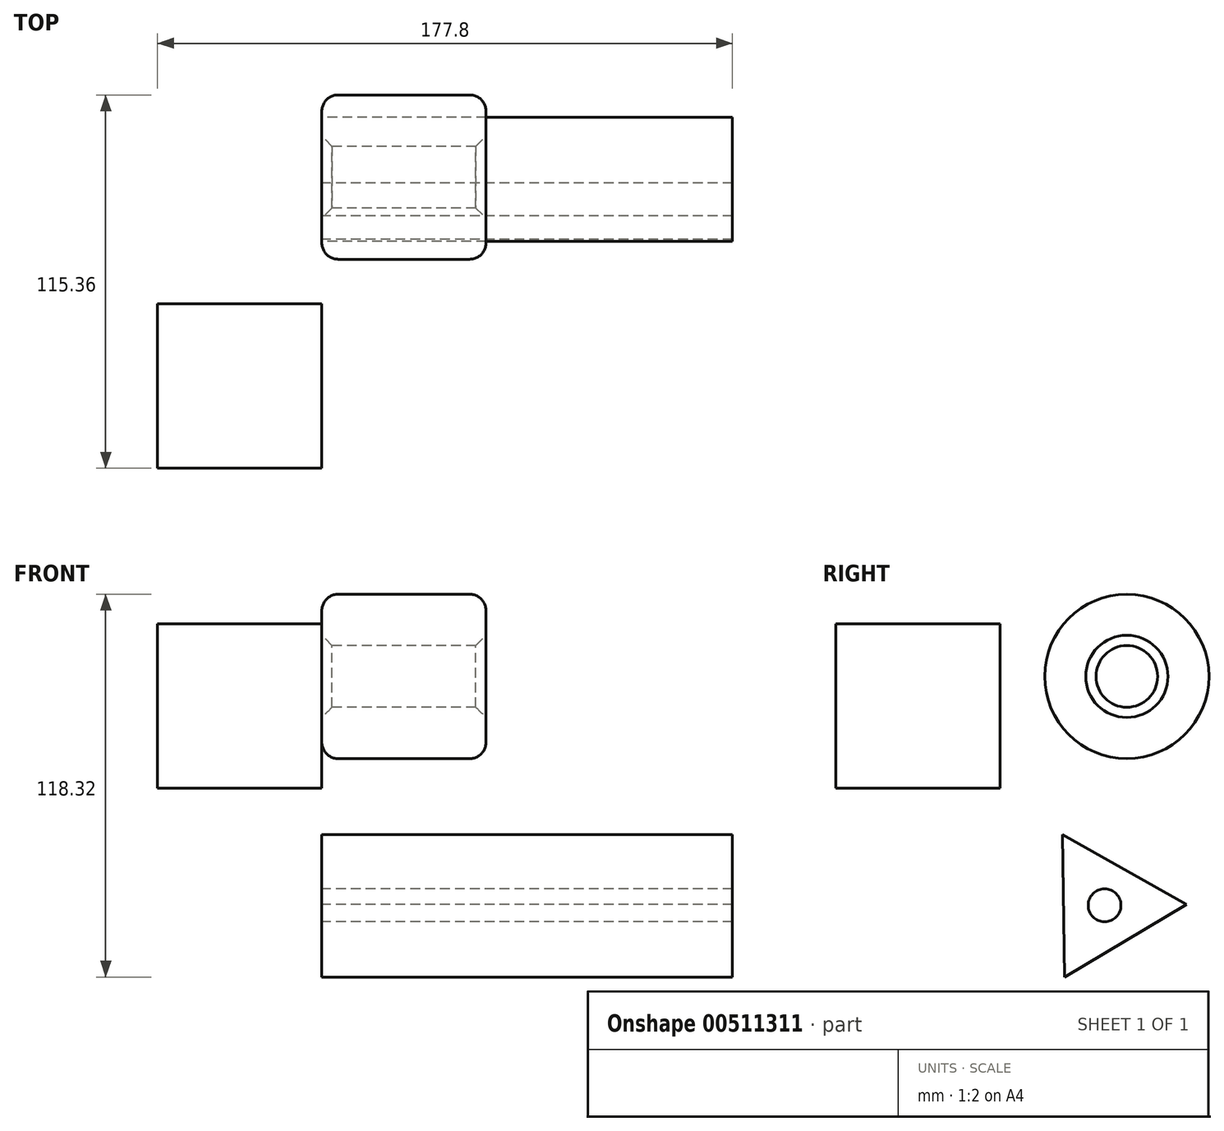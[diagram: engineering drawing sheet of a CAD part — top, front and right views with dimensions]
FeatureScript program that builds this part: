
annotation { "Feature Type Name" : "Feature", "Feature Type Description" : "" }
export const myFeature = defineFeature(function(context is Context, id is Id, definition is map)
    precondition{}
    {
        {
            var Q0;
            Q0=qCreatedBy(makeId("Front.planeOp"),FACE);
            var sketch = newSketch(context, id + "F0", { "sketchPlane" : qUnion([Q0])});
            skLineSegment(sketch, "E0", {"start": v(0, 0) * mm, "end": v(0, 50.8) * mm});
            skLineSegment(sketch, "E1", {"start": v(0, 50.8) * mm, "end": v(-50.8, 50.8) * mm});
            skLineSegment(sketch, "E2", {"start": v(-50.8, 50.8) * mm, "end": v(-50.8, 0) * mm});
            skLineSegment(sketch, "E3", {"start": v(-50.8, 0) * mm, "end": v(0, 0) * mm});
            skSolve(sketch);
        }
        {
            var Q0;
            Q0=makeQuery(id+"F0.imprint","IMPRINT",FACE,{"disambiguationData":[TD([[makeQuery(id+"F0.imprint","IMPRINT",EDGE,{"derivedFrom":sQuery(id+"F0.wireOp",EDGE,"E0")}),1.0]])]});
            extrude(context, id + "F1", {"entities" : qUnion([Q0]), "depth" : 50.8 * mm, "offsetDistance" : 25.4 * mm});
        }
        {
            var Q0;
            Q0=qCreatedBy(makeId("Right.planeOp"),FACE);
            var sketch = newSketch(context, id + "F2", { "sketchPlane" : qUnion([Q0])});
            skCircle(sketch, "E4", {"center": v(39.16, 34.5) * mm, "radius": 25.4 * mm});
            skLineSegment(sketch, "E5", {"start": v(39.16, 34.5) * mm, "end": v(64.56, 34.5) * mm});
            skLineSegment(sketch, "E6", {"start": v(39.16, 34.5) * mm, "end": v(13.76, 34.5) * mm});
            skLineSegment(sketch, "E7", {"start": v(39.16, 34.5) * mm, "end": v(39.16, 59.9) * mm});
            skLineSegment(sketch, "E8", {"start": v(39.16, 34.5) * mm, "end": v(39.16, 9.1) * mm});
            skCircle(sketch, "E9", {"center": v(39.16, 34.5) * mm, "radius": 9.53 * mm});
            skSolve(sketch);
        }
        {
            var Q0;
            Q0=makeQuery(id+"F2.imprint","IMPRINT",FACE,{"disambiguationData":[TD([[makeQuery(id+"F2.imprint","IMPRINT",EDGE,{"derivedFrom":sQuery(id+"F2.wireOp",EDGE,"E4")}),1.0]])]});
            extrude(context, id + "F3", {"entities" : qUnion([Q0]), "depth" : 50.8 * mm, "offsetDistance" : 25.4 * mm});
        }
        {
            var Q0;
            Q0=makeQuery(id+"F3.opExtrude","CAP_EDGE",EDGE,{"disambiguationData":[OSD([sQuery(id+"F2.wireOp",EDGE,"E4")])],"isStart":false});
            var Q1;
            Q1=makeQuery(id+"F3.opExtrude","CAP_EDGE",EDGE,{"disambiguationData":[OSD([sQuery(id+"F2.wireOp",EDGE,"E4")])],"isStart":true});
            fillet(context, id + "F4", {"entities" : qUnion([Q0, Q1]), "radius" : 5.08 * mm, "tangentPropagation" : true, "allowEdgeOverflow" : false});
        }
        {
            var Q0;
            Q0=makeQuery(id+"F3.opExtrude","CAP_EDGE",EDGE,{"disambiguationData":[OSD([sQuery(id+"F2.wireOp",EDGE,"E9")])],"isStart":true});
            chamfer(context, id + "F5", {"entities" : qUnion([Q0]), "width" : 3.17 * mm, "tangentPropagation" : true});
        }
        {
            var Q0;
            Q0=makeQuery(id+"F3.opExtrude","CAP_EDGE",EDGE,{"disambiguationData":[OSD([sQuery(id+"F2.wireOp",EDGE,"E9")])],"isStart":false});
            chamfer(context, id + "F6", {"entities" : qUnion([Q0]), "width" : 3.17 * mm, "tangentPropagation" : true});
        }
        {
            var Q0;
            Q0=qCreatedBy(makeId("Right.planeOp"),FACE);
            var sketch = newSketch(context, id + "F7", { "sketchPlane" : qUnion([Q0])});
            skCircle(sketch, "E10.cCircle", {"center": v(32.29, -36.26) * mm, "radius": 12.7 * mm, "construction": true});
            skLineSegment(sketch, "E10.0", {"start": v(57.68, -35.93) * mm, "end": v(19.87, -58.42) * mm});
            skLineSegment(sketch, "E10.1", {"start": v(19.87, -58.42) * mm, "end": v(19.3, -14.43) * mm});
            skLineSegment(sketch, "E10.2", {"start": v(19.3, -14.43) * mm, "end": v(57.68, -35.93) * mm});
            skPoint(sketch, "E10.0.midPoint", {"position": v(38.78, -47.17) * mm});
            skCircle(sketch, "E11", {"center": v(32.29, -36.26) * mm, "radius": 5.08 * mm});
            skSolve(sketch);
        }
        {
            var Q0;
            Q0 = qSketchRegion(id + "F7", true);
            extrude(context, id + "F8", {"entities" : qUnion([Q0]), "depth" : 127 * mm, "offsetDistance" : 25.4 * mm});
        }
    });
